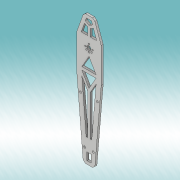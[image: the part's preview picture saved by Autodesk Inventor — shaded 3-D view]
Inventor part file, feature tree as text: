
AUTODESK INVENTOR PART (.ipt)
format: ipt  version: 2019 (Build 230136000, 136)  size: 211,968 bytes
history: native  units: mm
features: extrude x2
ambient origin geometry x8: Origin, YZ Plane, XZ Plane, XY Plane, X Axis, Y Axis, Z Axis, Center Point
bodies: Solid1 (feature_tree)
feature tree (2):
  extrude  "Extrusion1"  Depth=7.0mm
  extrude  "Extrusion2"  Depth=6.0mm
